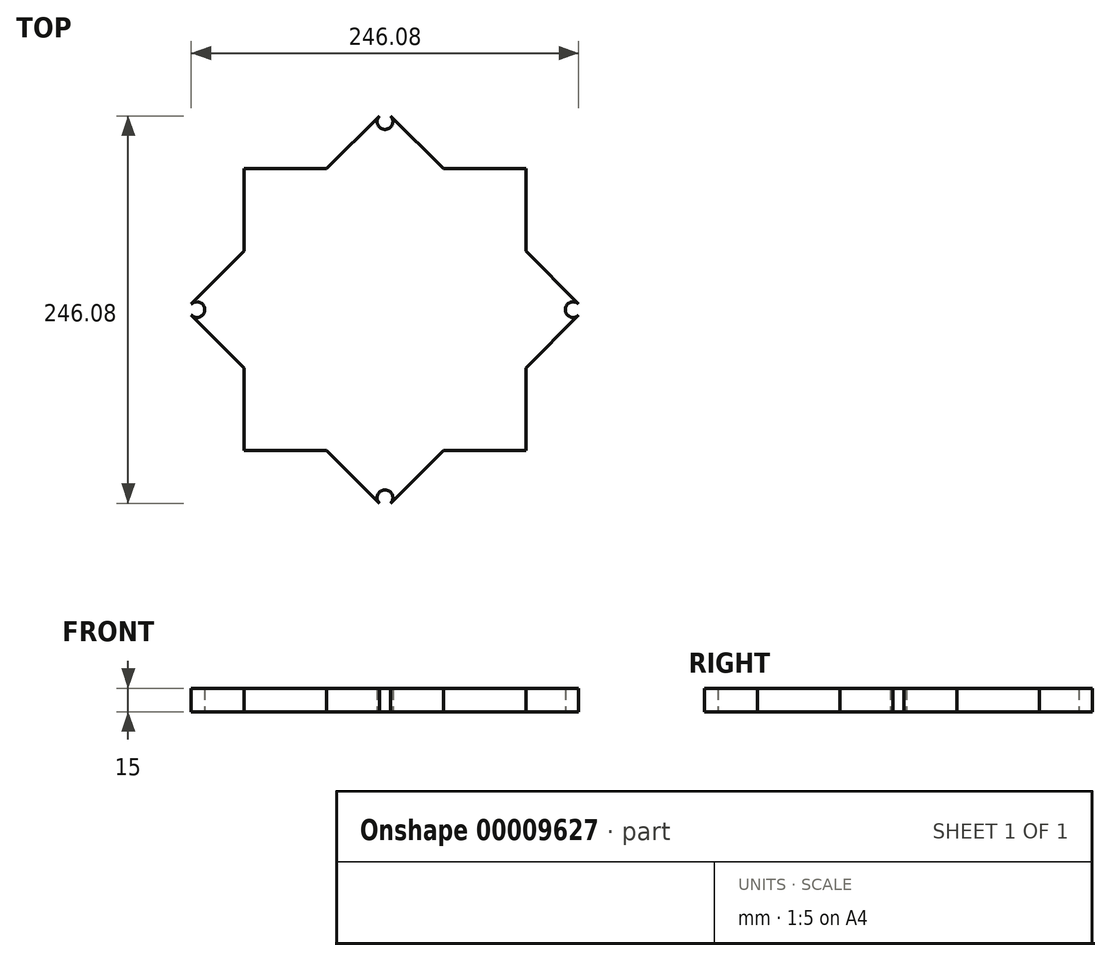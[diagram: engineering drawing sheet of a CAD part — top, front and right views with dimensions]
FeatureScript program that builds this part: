
annotation { "Feature Type Name" : "Feature", "Feature Type Description" : "" }
export const myFeature = defineFeature(function(context is Context, id is Id, definition is map)
    precondition{}
    {
        {
            var Q0;
            Q0=qCreatedBy(makeId("Top.planeOp"),FACE);
            var sketch = newSketch(context, id + "F0", { "sketchPlane" : qUnion([Q0])});
            skLineSegment(sketch, "E0.rect.bottom", {"start": v(89.5, 89.5) * mm, "end": v(-89.5, 89.5) * mm});
            skLineSegment(sketch, "E0.rect.top", {"start": v(89.5, -89.5) * mm, "end": v(-89.5, -89.5) * mm});
            skLineSegment(sketch, "E0.rect.left", {"start": v(89.5, 89.5) * mm, "end": v(89.5, -89.5) * mm});
            skLineSegment(sketch, "E0.rect.right", {"start": v(-89.5, 89.5) * mm, "end": v(-89.5, -89.5) * mm});
            skPoint(sketch, "E0.rect.middle", {"position": v(0, 0) * mm});
            skLineSegment(sketch, "E1", {"start": v(0, -124.5) * mm, "end": v(0, 124.5) * mm});
            skLineSegment(sketch, "E2", {"start": v(-124.5, 0) * mm, "end": v(124.5, 0) * mm});
            skPoint(sketch, "E2.endSnap0", {"position": v(89.5, 0) * mm});
            skLineSegment(sketch, "E3", {"start": v(0, 124.5) * mm, "end": v(0, 119.5) * mm});
            skLineSegment(sketch, "E4", {"start": v(-124.5, 0) * mm, "end": v(-119.5, 0) * mm});
            skLineSegment(sketch, "E5", {"start": v(0, -124.5) * mm, "end": v(0, -119.5) * mm});
            skLineSegment(sketch, "E6", {"start": v(124.5, 0) * mm, "end": v(119.5, 0) * mm});
            skCircle(sketch, "E7", {"center": v(119.5, 0) * mm, "radius": 5 * mm});
            skCircle(sketch, "E8", {"center": v(-119.5, 0) * mm, "radius": 5 * mm});
            skCircle(sketch, "E9", {"center": v(0, 119.5) * mm, "radius": 5 * mm});
            skCircle(sketch, "E10", {"center": v(0, -119.5) * mm, "radius": 5 * mm});
            skLineSegment(sketch, "E11", {"start": v(-123.04, 3.54) * mm, "end": v(-3.54, 123.04) * mm});
            skLineSegment(sketch, "E12", {"start": v(-123.04, -3.54) * mm, "end": v(-3.54, -123.04) * mm});
            skLineSegment(sketch, "E13", {"start": v(3.54, -123.04) * mm, "end": v(123.04, -3.54) * mm});
            skLineSegment(sketch, "E14", {"start": v(3.54, 123.04) * mm, "end": v(123.04, 3.54) * mm});
            skSolve(sketch);
        }
        {
            var Q0;
            {var subQ0=sQuery(id+"F0.wireOp",EDGE,"E11");var subQ1=sQuery(id+"F0.wireOp",EDGE,"E0.rect.right");var subQ2=makeQuery(id+"F0.imprint","INTERSECT",VERTEX,{"derivedFrom":[subQ1,subQ0]});Q0=makeQuery(id+"F0.imprint","IMPRINT",FACE,{"disambiguationData":[TD([[makeQuery(id+"F0.imprint","IMPRINT",EDGE,{"disambiguationData":[TD([[subQ2,-1.0]])],"derivedFrom":subQ1}),-1.0]])]});}
            var Q1;
            {var subQ0=sQuery(id+"F0.wireOp",EDGE,"E12");var subQ1=sQuery(id+"F0.wireOp",EDGE,"E0.rect.right");var subQ2=makeQuery(id+"F0.imprint","INTERSECT",VERTEX,{"derivedFrom":[subQ1,subQ0]});Q1=makeQuery(id+"F0.imprint","IMPRINT",FACE,{"disambiguationData":[TD([[makeQuery(id+"F0.imprint","IMPRINT",EDGE,{"disambiguationData":[TD([[subQ2,1.0]])],"derivedFrom":subQ1}),-1.0]])]});}
            var Q2;
            {var subQ1=sQuery(id+"F0.wireOp",EDGE,"E0.rect.right");var subQ3=sQuery(id+"F0.wireOp",EDGE,"E0.rect.bottom");var subQ5=makeQuery(id+"F0.imprint","INTERSECT",VERTEX,{"derivedFrom":[subQ3,subQ1]});Q2=makeQuery(id+"F0.imprint","IMPRINT",FACE,{"disambiguationData":[TD([[makeQuery(id+"F0.imprint","IMPRINT",EDGE,{"disambiguationData":[TD([[subQ5,1.0]])],"derivedFrom":subQ3}),1.0]])]});}
            var Q3;
            {var subQ0=sQuery(id+"F0.wireOp",EDGE,"E11");var subQ1=sQuery(id+"F0.wireOp",EDGE,"E0.rect.bottom");var subQ2=makeQuery(id+"F0.imprint","INTERSECT",VERTEX,{"derivedFrom":[subQ1,subQ0]});Q3=makeQuery(id+"F0.imprint","IMPRINT",FACE,{"disambiguationData":[TD([[makeQuery(id+"F0.imprint","IMPRINT",EDGE,{"disambiguationData":[TD([[subQ2,1.0]])],"derivedFrom":subQ1}),-1.0]])]});}
            var Q4;
            {var subQ0=sQuery(id+"F0.wireOp",EDGE,"E14");var subQ1=sQuery(id+"F0.wireOp",EDGE,"E0.rect.bottom");var subQ2=makeQuery(id+"F0.imprint","INTERSECT",VERTEX,{"derivedFrom":[subQ1,subQ0]});Q4=makeQuery(id+"F0.imprint","IMPRINT",FACE,{"disambiguationData":[TD([[makeQuery(id+"F0.imprint","IMPRINT",EDGE,{"disambiguationData":[TD([[subQ2,-1.0]])],"derivedFrom":subQ1}),-1.0]])]});}
            var Q5;
            {var subQ1=sQuery(id+"F0.wireOp",EDGE,"E0.rect.left");var subQ3=sQuery(id+"F0.wireOp",EDGE,"E0.rect.bottom");var subQ5=makeQuery(id+"F0.imprint","INTERSECT",VERTEX,{"derivedFrom":[subQ3,subQ1]});Q5=makeQuery(id+"F0.imprint","IMPRINT",FACE,{"disambiguationData":[TD([[makeQuery(id+"F0.imprint","IMPRINT",EDGE,{"disambiguationData":[TD([[subQ5,-1.0]])],"derivedFrom":subQ3}),1.0]])]});}
            var Q6;
            {var subQ0=sQuery(id+"F0.wireOp",EDGE,"E14");var subQ1=sQuery(id+"F0.wireOp",EDGE,"E0.rect.left");var subQ2=makeQuery(id+"F0.imprint","INTERSECT",VERTEX,{"derivedFrom":[subQ1,subQ0]});Q6=makeQuery(id+"F0.imprint","IMPRINT",FACE,{"disambiguationData":[TD([[makeQuery(id+"F0.imprint","IMPRINT",EDGE,{"disambiguationData":[TD([[subQ2,-1.0]])],"derivedFrom":subQ1}),1.0]])]});}
            var Q7;
            {var subQ0=sQuery(id+"F0.wireOp",EDGE,"E13");var subQ1=sQuery(id+"F0.wireOp",EDGE,"E0.rect.left");var subQ2=makeQuery(id+"F0.imprint","INTERSECT",VERTEX,{"derivedFrom":[subQ1,subQ0]});Q7=makeQuery(id+"F0.imprint","IMPRINT",FACE,{"disambiguationData":[TD([[makeQuery(id+"F0.imprint","IMPRINT",EDGE,{"disambiguationData":[TD([[subQ2,1.0]])],"derivedFrom":subQ1}),1.0]])]});}
            var Q8;
            {var subQ1=sQuery(id+"F0.wireOp",EDGE,"E0.rect.left");var subQ3=sQuery(id+"F0.wireOp",EDGE,"E0.rect.top");var subQ5=makeQuery(id+"F0.imprint","INTERSECT",VERTEX,{"derivedFrom":[subQ3,subQ1]});Q8=makeQuery(id+"F0.imprint","IMPRINT",FACE,{"disambiguationData":[TD([[makeQuery(id+"F0.imprint","IMPRINT",EDGE,{"disambiguationData":[TD([[subQ5,-1.0]])],"derivedFrom":subQ3}),-1.0]])]});}
            var Q9;
            {var subQ0=sQuery(id+"F0.wireOp",EDGE,"E13");var subQ1=sQuery(id+"F0.wireOp",EDGE,"E0.rect.top");var subQ2=makeQuery(id+"F0.imprint","INTERSECT",VERTEX,{"derivedFrom":[subQ1,subQ0]});Q9=makeQuery(id+"F0.imprint","IMPRINT",FACE,{"disambiguationData":[TD([[makeQuery(id+"F0.imprint","IMPRINT",EDGE,{"disambiguationData":[TD([[subQ2,-1.0]])],"derivedFrom":subQ1}),1.0]])]});}
            var Q10;
            {var subQ0=sQuery(id+"F0.wireOp",EDGE,"E12");var subQ1=sQuery(id+"F0.wireOp",EDGE,"E0.rect.top");var subQ2=makeQuery(id+"F0.imprint","INTERSECT",VERTEX,{"derivedFrom":[subQ1,subQ0]});Q10=makeQuery(id+"F0.imprint","IMPRINT",FACE,{"disambiguationData":[TD([[makeQuery(id+"F0.imprint","IMPRINT",EDGE,{"disambiguationData":[TD([[subQ2,1.0]])],"derivedFrom":subQ1}),1.0]])]});}
            var Q11;
            {var subQ1=sQuery(id+"F0.wireOp",EDGE,"E0.rect.right");var subQ3=sQuery(id+"F0.wireOp",EDGE,"E0.rect.top");var subQ5=makeQuery(id+"F0.imprint","INTERSECT",VERTEX,{"derivedFrom":[subQ3,subQ1]});Q11=makeQuery(id+"F0.imprint","IMPRINT",FACE,{"disambiguationData":[TD([[makeQuery(id+"F0.imprint","IMPRINT",EDGE,{"disambiguationData":[TD([[subQ5,1.0]])],"derivedFrom":subQ3}),-1.0]])]});}
            var Q12;
            {var subQ2=sQuery(id+"F0.wireOp",EDGE,"E5");Q12=makeQuery(id+"F0.imprint","IMPRINT",FACE,{"disambiguationData":[TD([[makeQuery(id+"F0.imprint","IMPRINT",EDGE,{"derivedFrom":subQ2}),1.0]])]});}
            var Q13;
            {var subQ4=sQuery(id+"F0.wireOp",EDGE,"E5");Q13=makeQuery(id+"F0.imprint","IMPRINT",FACE,{"disambiguationData":[TD([[makeQuery(id+"F0.imprint","IMPRINT",EDGE,{"derivedFrom":subQ4}),-1.0]])]});}
            var Q14;
            {var subQ2=sQuery(id+"F0.wireOp",EDGE,"E6");Q14=makeQuery(id+"F0.imprint","IMPRINT",FACE,{"disambiguationData":[TD([[makeQuery(id+"F0.imprint","IMPRINT",EDGE,{"derivedFrom":subQ2}),1.0]])]});}
            var Q15;
            {var subQ2=sQuery(id+"F0.wireOp",EDGE,"E6");Q15=makeQuery(id+"F0.imprint","IMPRINT",FACE,{"disambiguationData":[TD([[makeQuery(id+"F0.imprint","IMPRINT",EDGE,{"derivedFrom":subQ2}),-1.0]])]});}
            var Q16;
            {var subQ2=sQuery(id+"F0.wireOp",EDGE,"E4");Q16=makeQuery(id+"F0.imprint","IMPRINT",FACE,{"disambiguationData":[TD([[makeQuery(id+"F0.imprint","IMPRINT",EDGE,{"derivedFrom":subQ2}),1.0]])]});}
            var Q17;
            {var subQ4=sQuery(id+"F0.wireOp",EDGE,"E4");Q17=makeQuery(id+"F0.imprint","IMPRINT",FACE,{"disambiguationData":[TD([[makeQuery(id+"F0.imprint","IMPRINT",EDGE,{"derivedFrom":subQ4}),-1.0]])]});}
            var Q18;
            {var subQ0=sQuery(id+"F0.wireOp",EDGE,"E11");var subQ3=sQuery(id+"F0.wireOp",EDGE,"E0.rect.bottom");var subQ4=makeQuery(id+"F0.imprint","INTERSECT",VERTEX,{"derivedFrom":[subQ3,subQ0]});Q18=makeQuery(id+"F0.imprint","IMPRINT",FACE,{"disambiguationData":[TD([[makeQuery(id+"F0.imprint","IMPRINT",EDGE,{"disambiguationData":[TD([[subQ4,1.0]])],"derivedFrom":subQ3}),1.0]])]});}
            var Q19;
            {var subQ0=sQuery(id+"F0.wireOp",EDGE,"E14");var subQ3=sQuery(id+"F0.wireOp",EDGE,"E0.rect.bottom");var subQ4=makeQuery(id+"F0.imprint","INTERSECT",VERTEX,{"derivedFrom":[subQ3,subQ0]});Q19=makeQuery(id+"F0.imprint","IMPRINT",FACE,{"disambiguationData":[TD([[makeQuery(id+"F0.imprint","IMPRINT",EDGE,{"disambiguationData":[TD([[subQ4,-1.0]])],"derivedFrom":subQ3}),1.0]])]});}
            var Q20;
            {var subQ0=sQuery(id+"F0.wireOp",EDGE,"E13");var subQ3=sQuery(id+"F0.wireOp",EDGE,"E0.rect.top");var subQ4=makeQuery(id+"F0.imprint","INTERSECT",VERTEX,{"derivedFrom":[subQ3,subQ0]});Q20=makeQuery(id+"F0.imprint","IMPRINT",FACE,{"disambiguationData":[TD([[makeQuery(id+"F0.imprint","IMPRINT",EDGE,{"disambiguationData":[TD([[subQ4,-1.0]])],"derivedFrom":subQ3}),-1.0]])]});}
            var Q21;
            {var subQ0=sQuery(id+"F0.wireOp",EDGE,"E12");var subQ3=sQuery(id+"F0.wireOp",EDGE,"E0.rect.top");var subQ4=makeQuery(id+"F0.imprint","INTERSECT",VERTEX,{"derivedFrom":[subQ3,subQ0]});Q21=makeQuery(id+"F0.imprint","IMPRINT",FACE,{"disambiguationData":[TD([[makeQuery(id+"F0.imprint","IMPRINT",EDGE,{"disambiguationData":[TD([[subQ4,1.0]])],"derivedFrom":subQ3}),-1.0]])]});}
            var Q22;
            {var subQ4=sQuery(id+"F0.wireOp",EDGE,"E3");Q22=makeQuery(id+"F0.imprint","IMPRINT",FACE,{"disambiguationData":[TD([[makeQuery(id+"F0.imprint","IMPRINT",EDGE,{"derivedFrom":subQ4}),1.0]])]});}
            var Q23;
            {var subQ4=sQuery(id+"F0.wireOp",EDGE,"E3");Q23=makeQuery(id+"F0.imprint","IMPRINT",FACE,{"disambiguationData":[TD([[makeQuery(id+"F0.imprint","IMPRINT",EDGE,{"derivedFrom":subQ4}),-1.0]])]});}
            extrude(context, id + "F1", {"entities" : qUnion([Q0, Q1, Q2, Q3, Q4, Q5, Q6, Q7, Q8, Q9, Q10, Q11, Q12, Q13, Q14, Q15, Q16, Q17, Q18, Q19, Q20, Q21, Q22, Q23]), "depth" : 15 * mm});
        }
    });
